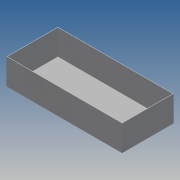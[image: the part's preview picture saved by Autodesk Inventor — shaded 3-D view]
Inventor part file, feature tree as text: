
AUTODESK INVENTOR PART (.ipt)
format: ipt  version: 2016 SP2 (Build 200236200, 236)  size: 89,600 bytes
history: native  units: mm
features: extrude x1, shell x1, sketch x1
ambient origin geometry x8: Origin, YZ Plane, XZ Plane, XY Plane, X Axis, Y Axis, Z Axis, Center Point
bodies: Solid1 (feature_tree)
feature tree (3):
  extrude  "Extrusion1"  Depth=100.0mm
  shell  "Shell1"  Thickness=50.0mm
  sketch  "Sketch1"  dims[d0=225.0mm d1=100.0mm d2=50.0mm d3=0.0mm d4=1.0mm]
